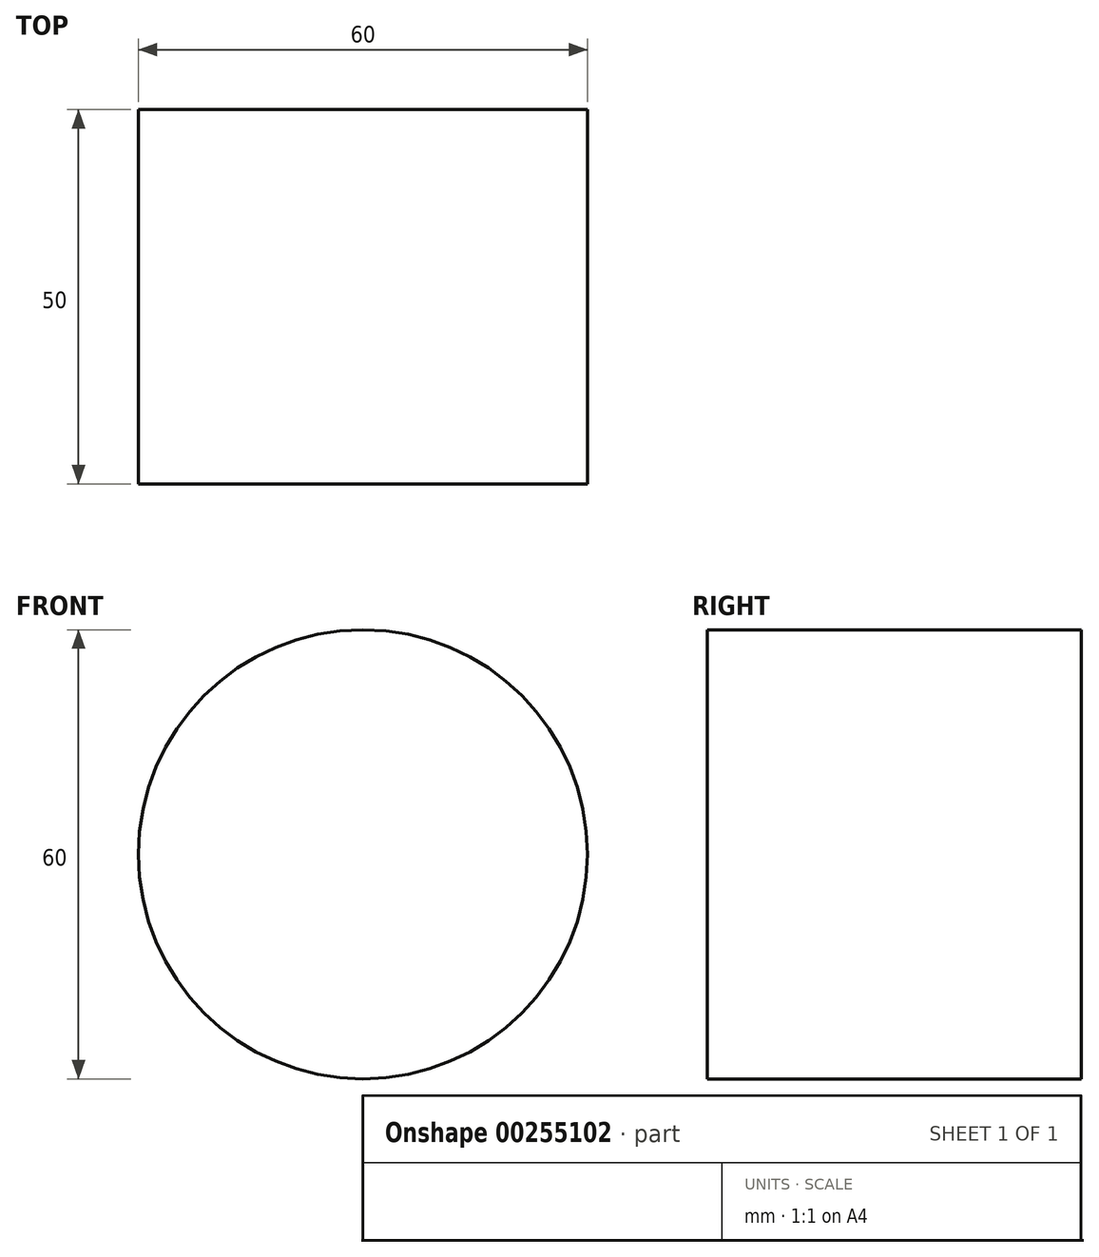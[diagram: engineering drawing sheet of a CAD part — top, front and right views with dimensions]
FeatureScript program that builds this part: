
annotation { "Feature Type Name" : "Feature", "Feature Type Description" : "" }
export const myFeature = defineFeature(function(context is Context, id is Id, definition is map)
    precondition{}
    {
        {
            var Q0;
            Q0=qCreatedBy(makeId("Front.planeOp"),FACE);
            var sketch = newSketch(context, id + "F0", { "sketchPlane" : qUnion([Q0])});
            skCircle(sketch, "E0", {"center": v(0, 0) * mm, "radius": 30 * mm});
            skSolve(sketch);
        }
        {
            var Q0;
            Q0 = qSketchRegion(id + "F0", true);
            var Q1;
            Q1=makeQuery(id+"F0.imprint","IMPRINT",FACE,{"disambiguationData":[TD([[makeQuery(id+"F0.imprint","IMPRINT",EDGE,{"derivedFrom":sQuery(id+"F0.wireOp",EDGE,"E0")}),1.0]])]});
            extrude(context, id + "F1", {"entities" : qUnion([Q0, Q1]), "depth" : 50 * mm});
        }
    });
